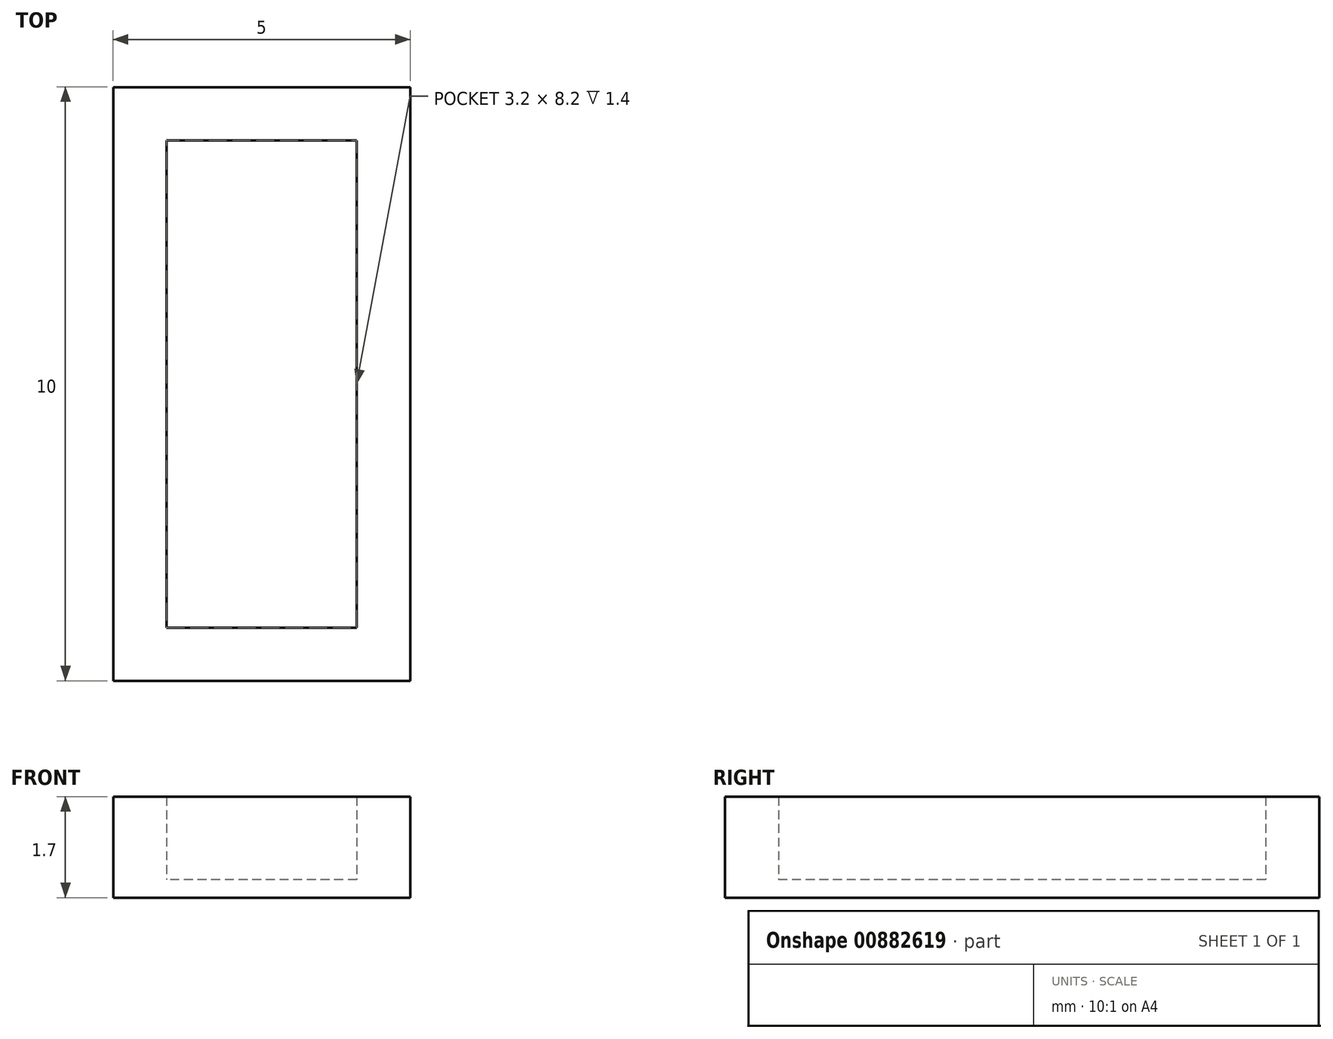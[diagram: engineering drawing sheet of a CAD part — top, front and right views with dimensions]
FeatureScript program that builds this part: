
annotation { "Feature Type Name" : "Feature", "Feature Type Description" : "" }
export const myFeature = defineFeature(function(context is Context, id is Id, definition is map)
    precondition{}
    {
        {
            var Q0;
            Q0=qCreatedBy(makeId("Top.planeOp"),FACE);
            var sketch = newSketch(context, id + "F0", { "sketchPlane" : qUnion([Q0])});
            skLineSegment(sketch, "E0.bottom", {"start": v(-1.74, 3.76) * mm, "end": v(3.26, 3.76) * mm});
            skLineSegment(sketch, "E0.top", {"start": v(-1.74, -6.24) * mm, "end": v(3.26, -6.24) * mm});
            skLineSegment(sketch, "E0.left", {"start": v(-1.74, 3.76) * mm, "end": v(-1.74, -6.24) * mm});
            skLineSegment(sketch, "E0.right", {"start": v(3.26, 3.76) * mm, "end": v(3.26, -6.24) * mm});
            skSolve(sketch);
        }
        {
            var Q0;
            Q0=makeQuery(id+"F0.imprint","IMPRINT",FACE,{"disambiguationData":[TD([[makeQuery(id+"F0.imprint","IMPRINT",EDGE,{"derivedFrom":sQuery(id+"F0.wireOp",EDGE,"E0.bottom")}),-1.0]])]});
            extrude(context, id + "F1", {"entities" : qUnion([Q0]), "depth" : 0.3 * mm, "offsetDistance" : 25 * mm});
        }
        {
            var Q0;
            Q0=makeQuery(id+"F1.opExtrude","CAP_FACE",FACE,{"disambiguationData":[OSD([sQuery(id+"F0.wireOp",EDGE,"E0.bottom"),sQuery(id+"F0.wireOp",EDGE,"E0.top"),sQuery(id+"F0.wireOp",EDGE,"E0.left"),sQuery(id+"F0.wireOp",EDGE,"E0.right")])],"isStart":false});
            var sketch = newSketch(context, id + "F2", { "sketchPlane" : qUnion([Q0])});
            skLineSegment(sketch, "E1.bottom", {"start": v(-1.74, 3.76) * mm, "end": v(3.26, 3.76) * mm});
            skLineSegment(sketch, "E1.top", {"start": v(-1.74, -6.24) * mm, "end": v(3.26, -6.24) * mm});
            skLineSegment(sketch, "E1.left", {"start": v(-1.74, 3.76) * mm, "end": v(-1.74, -6.24) * mm});
            skLineSegment(sketch, "E1.right", {"start": v(3.26, 3.76) * mm, "end": v(3.26, -6.24) * mm});
            skLineSegment(sketch, "E2.0", {"start": v(-0.84, 2.86) * mm, "end": v(-0.84, -5.34) * mm});
            skLineSegment(sketch, "E2.1", {"start": v(2.36, 2.86) * mm, "end": v(-0.84, 2.86) * mm});
            skLineSegment(sketch, "E2.2", {"start": v(2.36, -5.34) * mm, "end": v(2.36, 2.86) * mm});
            skLineSegment(sketch, "E2.3", {"start": v(-0.84, -5.34) * mm, "end": v(2.36, -5.34) * mm});
            skSolve(sketch);
        }
        {
            var Q0;
            Q0=makeQuery(id+"F2.imprint","IMPRINT",FACE,{"disambiguationData":[TD([[makeQuery(id+"F2.imprint","IMPRINT",EDGE,{"derivedFrom":sQuery(id+"F2.wireOp",EDGE,"E1.bottom")}),-1.0]])]});
            extrude(context, id + "F3", {"entities" : qUnion([Q0]), "operationType" : NewBodyOperationType.ADD, "depth" : 1.4 * mm, "offsetDistance" : 25 * mm});
        }
    });
